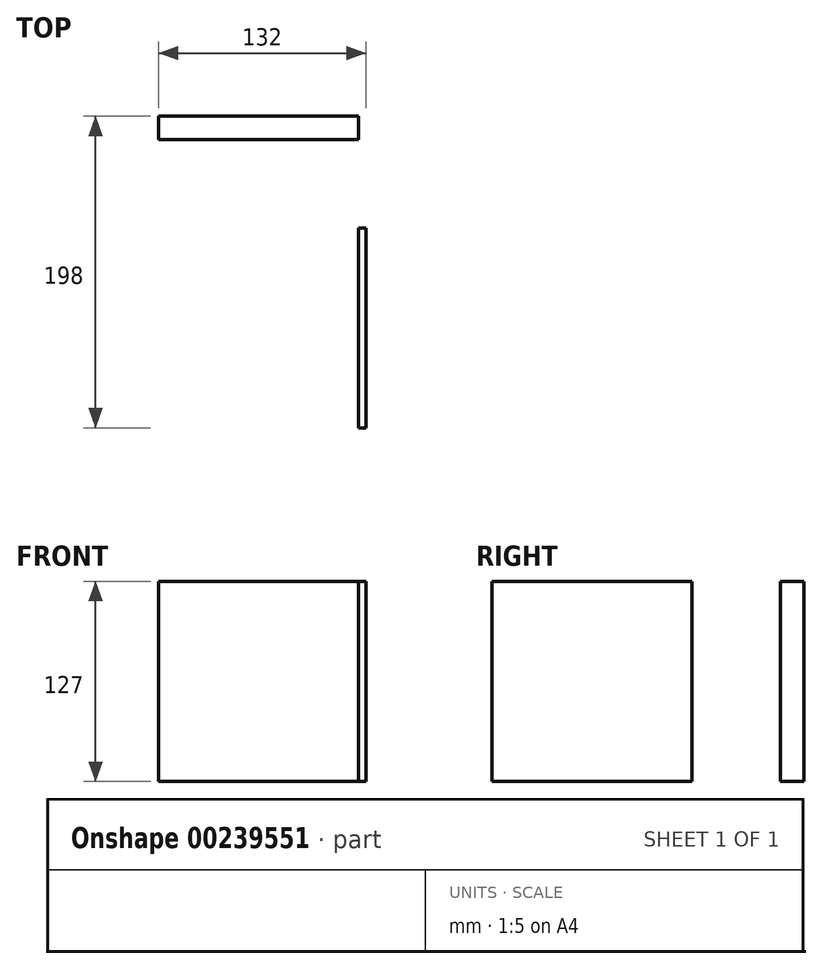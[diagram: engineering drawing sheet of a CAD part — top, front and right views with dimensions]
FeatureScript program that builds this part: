
annotation { "Feature Type Name" : "Feature", "Feature Type Description" : "" }
export const myFeature = defineFeature(function(context is Context, id is Id, definition is map)
    precondition{}
    {
        {
            assignVariable(context, id + "F0", {"name" : "L", "anyValue" : 5});
        }
        {
            var Q0;
            Q0=qCreatedBy(makeId("Front.planeOp"),FACE);
            var sketch = newSketch(context, id + "F1", { "sketchPlane" : qUnion([Q0])});
            skLineSegment(sketch, "E0.bottom", {"start": v(63.5, 63.5) * mm, "end": v(-63.5, 63.5) * mm});
            skLineSegment(sketch, "E0.top", {"start": v(63.5, -63.5) * mm, "end": v(-63.5, -63.5) * mm});
            skLineSegment(sketch, "E0.left", {"start": v(63.5, 63.5) * mm, "end": v(63.5, -63.5) * mm});
            skLineSegment(sketch, "E0.right", {"start": v(-63.5, 63.5) * mm, "end": v(-63.5, -63.5) * mm});
            skPoint(sketch, "E0.middle", {"position": v(0, 0) * mm});
            skSolve(sketch);
        }
        {
            var Q0;
            Q0 = qSketchRegion(id + "F1", true);
            extrude(context, id + "F2", {"entities" : qUnion([Q0]), "endBound" : BoundingType.SYMMETRIC, "depth" : (getVariable(context, 'L') * 3) * mm});
        }
        {
            var Q0;
            Q0=makeQuery(id+"F2.opExtrude","SWEPT_FACE",FACE,{"disambiguationData":[OSD([sQuery(id+"F1.wireOp",EDGE,"E0.left")])]});
            var sketch = newSketch(context, id + "F3", { "sketchPlane" : qUnion([Q0])});
            skLineSegment(sketch, "E1.bottom", {"start": v(-190.5, 63.5) * mm, "end": v(-63.5, 63.5) * mm});
            skLineSegment(sketch, "E1.top", {"start": v(-190.5, -63.5) * mm, "end": v(-63.5, -63.5) * mm});
            skLineSegment(sketch, "E1.left", {"start": v(-190.5, 63.5) * mm, "end": v(-190.5, -63.5) * mm});
            skLineSegment(sketch, "E1.right", {"start": v(-63.5, 63.5) * mm, "end": v(-63.5, -63.5) * mm});
            skSolve(sketch);
        }
        {
            var Q0;
            Q0 = qSketchRegion(id + "F3", true);
            extrude(context, id + "F4", {"entities" : qUnion([Q0]), "operationType" : NewBodyOperationType.ADD, "depth" : (getVariable(context, 'L')) * mm});
        }
    });
